# Revit family: LIANO II BATHROOM SHELF
name_source: partatom
category: Specialty Equipment
units: mm (PartAtom-declared; Revit-internal decimal feet)

## family parameters
Cut with Voids When Loaded = No
Host = Face
OmniClass Number = 23.40.20.21
OmniClass Title = Toilet and Bath Specialties
Part Type = Normal
Room Calculation Point = No
Round Connector Dimension = Use Radius
Shared = No

## types (6) — shared parameters
Assembly Code = C1030220
Default Elevation = 1000 mm  [stored 3.28084 ft]
Manufacturer = GWA Bathrooms & Kitchens
URL = https://www.caroma.com.au

## per-type parameters (varying)
| type | Material_Base | Model |
| LIANO II BATHROOM SHELF - CHROME | GWA_Metal-Chrome | 96449C |
| LIANO II BATHROOM SHELF - MATTE BLACK | GWA-Metal-Black | 96449B |
| LIANO II BATHROOM SHELF - BRUSHED NICKEL | GWA_Metal-Brushed-Nickel | 96449BN |
| LIANO II BATHROOM SHELF - BRUSHED BRASS | GWA_Metal-Brushed-Brass | 96449BB |
| LIANO II BATHROOM SHELF - GUNMETAL | GWA-Metal-Gunmetal Grey | 96449GM |
| LIANO II BATHROOM SHELF - BRUSHED BRONZE | GWA_Metal-Brushed-Bronze | 96449BBZ |

note: column(s) folded — value = type name in every type: Description

note: [stored X ft] marks values corroborated as IEEE doubles in the binary element streams (Revit-internal decimal feet)

## geometry (parser evidence)
native form markers: Sweep x2
no freeform markers — native parametric forms only
